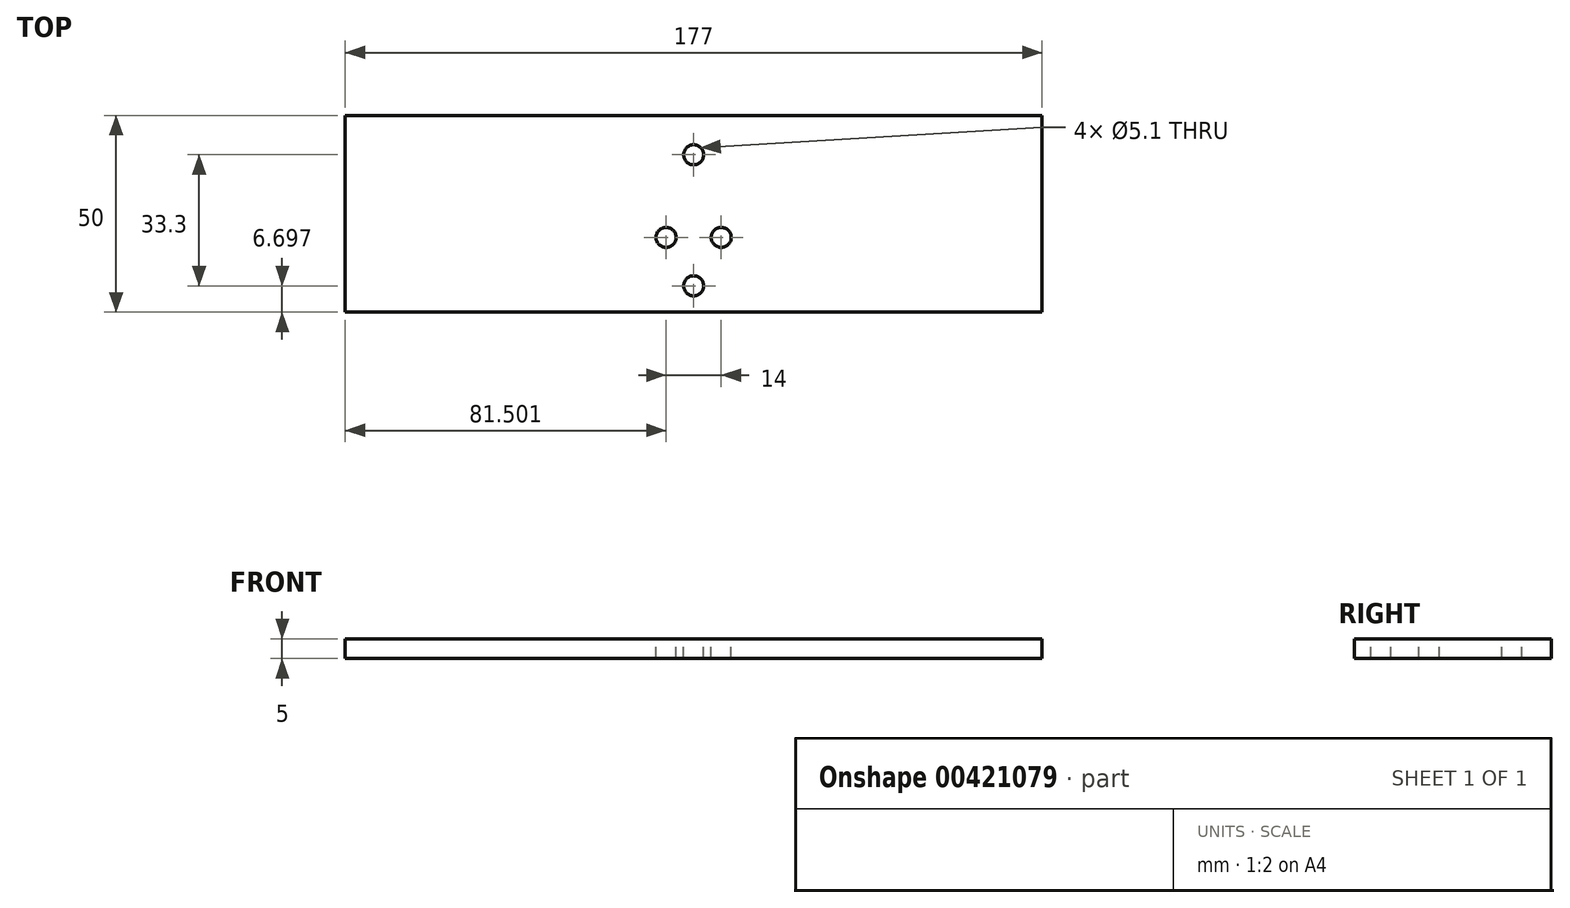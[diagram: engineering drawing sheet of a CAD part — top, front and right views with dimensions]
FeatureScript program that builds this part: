
annotation { "Feature Type Name" : "Feature", "Feature Type Description" : "" }
export const myFeature = defineFeature(function(context is Context, id is Id, definition is map)
    precondition{}
    {
        {
            var Q0;
            Q0=qCreatedBy(makeId("Top.planeOp"),FACE);
            var sketch = newSketch(context, id + "F0", { "sketchPlane" : qUnion([Q0])});
            skLineSegment(sketch, "E0.bottom", {"start": v(-92.32, 58.53) * mm, "end": v(84.68, 58.53) * mm});
            skLineSegment(sketch, "E0.top", {"start": v(-44.32, 8.53) * mm, "end": v(36.68, 8.53) * mm});
            skLineSegment(sketch, "E0.left", {"start": v(-92.32, 58.53) * mm, "end": v(-92.32, 8.53) * mm});
            skLineSegment(sketch, "E0.right", {"start": v(84.68, 58.53) * mm, "end": v(84.68, 8.53) * mm});
            skPoint(sketch, "E1.visualSharp", {"position": v(-54.32, 8.53) * mm});
            skPoint(sketch, "E2.visualSharp", {"position": v(46.68, 8.53) * mm});
            skLineSegment(sketch, "E3.top", {"start": v(-92.32, 8.53) * mm, "end": v(-44.32, 8.53) * mm});
            skLineSegment(sketch, "E4.trimOffspring", {"start": v(36.68, 8.53) * mm, "end": v(84.68, 8.53) * mm});
            skSolve(sketch);
        }
        {
            var Q0;
            Q0=qSketchRegion(id+"F0",true);
            extrude(context, id + "F1", {"entities" : qUnion([Q0]), "depth" : 5 * mm});
        }
        {
            var Q0;
            Q0=makeQuery(id+"F1.opExtrude","CAP_FACE",FACE,{"disambiguationData":[OSD([sQuery(id+"F0.wireOp",EDGE,"E0.bottom"),sQuery(id+"F0.wireOp",EDGE,"E0.top"),sQuery(id+"F0.wireOp",EDGE,"E0.left"),sQuery(id+"F0.wireOp",EDGE,"E0.right")])],"isStart":false});
            var sketch = newSketch(context, id + "F2", { "sketchPlane" : qUnion([Q0])});
            skPoint(sketch, "E5", {"position": v(-3.82, 48.53) * mm});
            skPoint(sketch, "E6", {"position": v(-3.82, 15.23) * mm});
            skPoint(sketch, "E7", {"position": v(-10.82, 27.53) * mm});
            skPoint(sketch, "E8", {"position": v(3.18, 27.53) * mm});
            skSolve(sketch);
        }
        {
            var Q0;
            Q0=sQuery(id+"F2.wireOp",VERTEX,"E7");
            var Q1;
            Q1=sQuery(id+"F2.wireOp",VERTEX,"E5");
            var Q2;
            Q2=sQuery(id+"F2.wireOp",VERTEX,"E8");
            var Q3;
            Q3=sQuery(id+"F2.wireOp",VERTEX,"E6");
            var Q4;
            Q4=makeQuery(id+"F1.opExtrude","SWEPT_BODY",BODY,{"disambiguationData":[OSD([sQuery(id+"F0.wireOp",EDGE,"E0.bottom"),sQuery(id+"F0.wireOp",EDGE,"E0.top"),sQuery(id+"F0.wireOp",EDGE,"E0.left"),sQuery(id+"F0.wireOp",EDGE,"E0.right")])]});
            hole(context, id + "F3", {"style" : HoleStyle.SIMPLE, "endStyle" : HoleEndStyle.THROUGH, "standardTappedOrClearance" : lookupTablePath({ "standard" : "ISO", "size" : "5.1", "type" : "Drilled" }), "standardBlindInLast" : lookupTablePath({ "standard" : "ISO", "size" : "5.1", "type" : "Drilled" }), "holeDiameter" : 5.1 * mm, "tappedDepth" : 12.7 * mm, "tapClearance" : 3, "locations" : qUnion([Q0, Q1, Q2, Q3]), "scope" : qUnion([Q4])});
        }
        {
            var Q0;
            Q0=makeQuery(id+"F1.opExtrude","CAP_FACE",FACE,{"disambiguationData":[OSD([sQuery(id+"F0.wireOp",EDGE,"E0.bottom"),sQuery(id+"F0.wireOp",EDGE,"E0.top"),sQuery(id+"F0.wireOp",EDGE,"E0.left"),sQuery(id+"F0.wireOp",EDGE,"E0.right"),sQuery(id+"F0.wireOp",EDGE,"dZqkjxpI-EO60-ojq4-aSAP-z9EactTdVXkJ.top"),sQuery(id+"F0.wireOp",EDGE,"dZqkjxpI-EO60-ojq4-aSAP-z9EactTdVXkJ.left"),sQuery(id+"F0.wireOp",EDGE,"dZqkjxpI-EO60-ojq4-aSAP-z9EactTdVXkJ.right"),sQuery(id+"F0.wireOp",EDGE,"G1G04smf-gb6x-Jy3t-V2pP-QACszAf4anMR.top"),sQuery(id+"F0.wireOp",EDGE,"G1G04smf-gb6x-Jy3t-V2pP-QACszAf4anMR.left"),sQuery(id+"F0.wireOp",EDGE,"G1G04smf-gb6x-Jy3t-V2pP-QACszAf4anMR.right"),sQuery(id+"F0.wireOp",EDGE,"E1.filletArc"),sQuery(id+"F0.wireOp",EDGE,"E2.filletArc")])],"isStart":false});
            var sketch = newSketch(context, id + "F4", { "sketchPlane" : qUnion([Q0])});
            skPoint(sketch, "E9", {"position": v(-73.32, -43.97) * mm});
            skPoint(sketch, "E10", {"position": v(65.68, -43.97) * mm});
            skPoint(sketch, "E11", {"position": v(-83.32, -14.47) * mm});
            skPoint(sketch, "E12", {"position": v(75.68, -6.47) * mm});
            skCircle(sketch, "E13", {"center": v(-63.32, -6.47) * mm, "radius": 2.1 * mm});
            skCircle(sketch, "E14", {"center": v(55.68, -14.47) * mm, "radius": 2.1 * mm});
            skCircle(sketch, "E15", {"center": v(-83.32, -14.47) * mm, "radius": 2.1 * mm});
            skCircle(sketch, "E16", {"center": v(-73.32, -43.97) * mm, "radius": 2.1 * mm});
            skCircle(sketch, "E17", {"center": v(75.68, -6.47) * mm, "radius": 2.1 * mm});
            skCircle(sketch, "E18", {"center": v(65.68, -43.97) * mm, "radius": 2.1 * mm});
            skSolve(sketch);
        }
        {
            var Q0;
            Q0=qSketchRegion(id+"F4",true);
            extrude(context, id + "F5", {"entities" : qUnion([Q0]), "operationType" : NewBodyOperationType.REMOVE, "oppositeDirection" : true, "depth" : 25 * mm});
        }
    });
